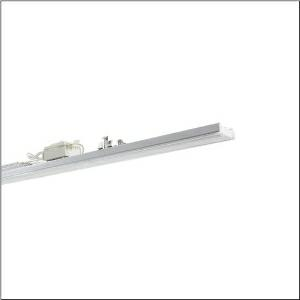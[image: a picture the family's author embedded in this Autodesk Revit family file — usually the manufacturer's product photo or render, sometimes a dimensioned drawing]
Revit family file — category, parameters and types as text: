
# Revit family: licross_r__21_recessed_ho_52te12dv4l2md_2c6d
name_source: partatom
category: Lighting Fixtures
units: mm (PartAtom-declared; Revit-internal decimal feet)

## family parameters
Cut with Voids When Loaded = No
Host = Face
Light Source = No
Part Type = Normal
Room Calculation Point = No
Round Connector Dimension = Use Diameter
Shared = No

## types (1)
- --- (1 x LED, 22710 lm, 125.6 W, 4000K)
    Apparent Load = 126 VA
    CIE Flux Codes = 69 91 98 100 100
    Color Rendering = 80
    Color Temperature = 4000K
    Default Elevation = 1800 mm
    Description = Licross® 21 Recessed HO, luminaire insert, of sheet steel, galvanised, coil coated, white, length: 2.250mm, width: 66mm, height: 67mm, LED rated luminous flux: 22.710lm, light colour: 840, control gear: DALI 2 (for two DALI lines), with plug, 6-pole, with phase selection, mains connection: 220..240V, AC/DC, 0/50..60Hz, rated input power: 126W, without changeover relay, for emergency light function, for central battery installations according to DIN EN 60598-2-22, halogen-free wiring, primary optical cover: cover, of PMMA, light emission: direct distribution, primary light characteristic: symmetric, protection rating (complete): IP54, insulation class (complete): insulation class I (protective earthing), certification: CE, ENEC, VDE, UKCA, protection symbol: D if used in an environment with non-conductive dust loads with corresponding accessories, impact resistance: IK06, permissible ambient temperature for indoor applications: -40..+30°C, standard: EN 60598-2-22, corresponds to IFS (International Featured Standards) requirements for safety and quality in the food industry, reducing of maximum allowable ambient temperature of 5°C with ceiling mounting, LABS conformity tested according to VDMA 24364:2018-05, packaging unit: 1 piece
    Height = 58 mm
    Lamp = 1 x LED
    Lamp Light Flux = 22710 lm
    Lamp Power = 125.6 W
    Lamp count = 1
    Length = 2250 mm
    Luminous efficacy = 181 lm/W
    Manufacturer = Siteco
    ModVariant = No
    Model = 52TE12DV4L2MD
    Mounting Place = Ceiling
    Mounting Type = Pendant
    Number of Poles = 1
    OnlyDefault = Yes
    Power Factor = 1
    Product Name = Licross® 21 Recessed HO
    Product group = luminaire insert
    ProductGroupID = 902
    Protection Class = Protection class I
    Protection Degree = IP 54
    RLX_Detail_Level = 1
    RLX_Emergency_Light_Flux = 0 lm
    RLX_Emergency_Type = 0
    RLX_Emergency_Type_DB = No
    RlxData = <blob elided: 30129 chars, md5=43c8cf58>
    Socket = socket
    Standby Power = 0 W
    System Light Flux = 22710 lm
    System Power = 126 W
    Type Comments = : AC-mode, luminous flux: 100 % | dim-lin: 254 | 489 mA
    Type Image = l_1296930.jpg
    URL = http://relux.com
    VarID = @adj_111682
    Voltage = 0 V
    Weight = 0.00 kg
    Width = 66 mm

## geometry (parser evidence)
native form markers: Blend x4, Sweep x11
no freeform markers — native parametric forms only
